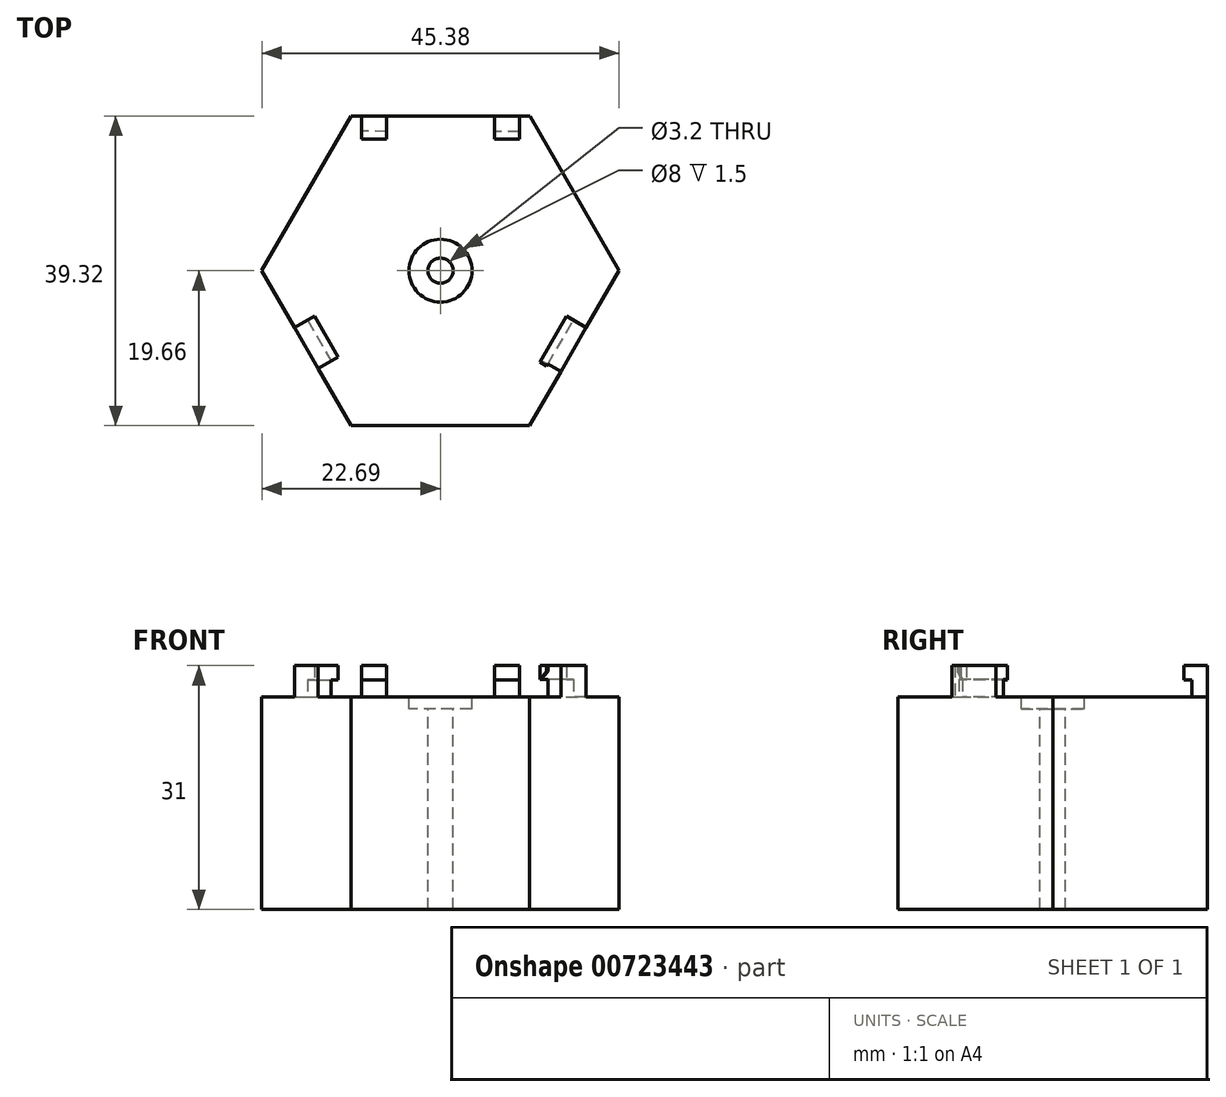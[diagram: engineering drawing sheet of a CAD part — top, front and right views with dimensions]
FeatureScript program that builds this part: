
annotation { "Feature Type Name" : "Feature", "Feature Type Description" : "" }
export const myFeature = defineFeature(function(context is Context, id is Id, definition is map)
    precondition{}
    {
        {
            var Q0;
            Q0=qCreatedBy(makeId("Top.planeOp"),FACE);
            var sketch = newSketch(context, id + "F0", { "sketchPlane" : qUnion([Q0])});
            skCircle(sketch, "E0.cCircle", {"center": v(0, 0) * mm, "radius": 17.65 * mm, "construction": true});
            skLineSegment(sketch, "E0.0", {"start": v(20.38, 0) * mm, "end": v(10.19, -17.66) * mm});
            skLineSegment(sketch, "E0.1", {"start": v(10.19, -17.66) * mm, "end": v(-10.2, -17.65) * mm});
            skLineSegment(sketch, "E0.2", {"start": v(-10.2, -17.65) * mm, "end": v(-20.38, 0) * mm});
            skLineSegment(sketch, "E0.3", {"start": v(-20.38, 0) * mm, "end": v(-10.19, 17.66) * mm});
            skLineSegment(sketch, "E0.4", {"start": v(-10.19, 17.66) * mm, "end": v(-6.75, 17.66) * mm});
            skLineSegment(sketch, "E0.5", {"start": v(10.2, 17.65) * mm, "end": v(20.39, 0) * mm});
            skPoint(sketch, "E0.0.midPoint", {"position": v(15.29, -8.83) * mm});
            skPoint(sketch, "E1", {"position": v(0, 17.65) * mm});
            skPoint(sketch, "E2", {"position": v(-10.19, 17.66) * mm});
            skPoint(sketch, "E3", {"position": v(10.2, 17.65) * mm});
            skLineSegment(sketch, "E4.top", {"start": v(6.75, 24.35) * mm, "end": v(-6.75, 24.35) * mm});
            skLineSegment(sketch, "E4.right", {"start": v(-6.75, 17.66) * mm, "end": v(-6.75, 24.35) * mm});
            skPoint(sketch, "E5.orphan", {"position": v(-6.75, 10.95) * mm});
            skLineSegment(sketch, "E6.trimOffspring", {"start": v(6.75, 17.65) * mm, "end": v(6.75, 24.35) * mm});
            skPoint(sketch, "E4.left.start.orphan", {"position": v(6.75, 10.95) * mm});
            skLineSegment(sketch, "E7.trimOffspring", {"start": v(6.75, 17.65) * mm, "end": v(10.2, 17.65) * mm});
            skLineSegment(sketch, "E8.trimOffspring", {"start": v(0, 17.65) * mm, "end": v(0, 17.65) * mm});
            skSolve(sketch);
        }
        {
            var Q0;
            Q0=qSketchRegion(id+"F0",true);
            extrude(context, id + "F1", {"entities" : qUnion([Q0]), "depth" : 1 * mm, "offsetDistance" : 25 * mm});
        }
        {
            var Q0;
            Q0=makeQuery(id+"F1.opExtrude","CAP_FACE",FACE,{"disambiguationData":[OSD([sQuery(id+"F0.wireOp",EDGE,"E0.0"),sQuery(id+"F0.wireOp",EDGE,"E0.1"),sQuery(id+"F0.wireOp",EDGE,"E0.2"),sQuery(id+"F0.wireOp",EDGE,"E0.3"),sQuery(id+"F0.wireOp",EDGE,"E0.4"),sQuery(id+"F0.wireOp",EDGE,"E0.5"),sQuery(id+"F0.wireOp",EDGE,"E4.top"),sQuery(id+"F0.wireOp",EDGE,"E4.right"),sQuery(id+"F0.wireOp",EDGE,"E6.trimOffspring"),sQuery(id+"F0.wireOp",EDGE,"E7.trimOffspring")])],"isStart":false});
            var sketch = newSketch(context, id + "F2", { "sketchPlane" : qUnion([Q0])});
            skPoint(sketch, "E9.0.midPoint", {"position": v(0, 13.44) * mm});
            skPoint(sketch, "E9.5.end.orphan", {"position": v(-7.76, 13.44) * mm});
            skPoint(sketch, "E10.orphan", {"position": v(-7.76, -13.44) * mm});
            skPoint(sketch, "E9.cCircle.center.orphan", {"position": v(0, 0) * mm});
            skPoint(sketch, "E9.0.end.orphan", {"position": v(7.76, 13.44) * mm});
            skLineSegment(sketch, "E11.0", {"start": v(18.94, 2.5) * mm, "end": v(16.44, 6.82) * mm});
            skLineSegment(sketch, "E11.3", {"start": v(-7.3, -17.65) * mm, "end": v(-2.3, -17.65) * mm});
            skLineSegment(sketch, "E11.5", {"start": v(-11.63, 15.16) * mm, "end": v(-14.13, 10.83) * mm});
            skLineSegment(sketch, "E12.0", {"start": v(14.61, 0) * mm, "end": v(12.11, 4.33) * mm});
            skLineSegment(sketch, "E12.3", {"start": v(-7.3, -12.65) * mm, "end": v(-2.3, -12.65) * mm});
            skLineSegment(sketch, "E12.5", {"start": v(-7.3, 12.66) * mm, "end": v(-9.8, 8.33) * mm});
            skLineSegment(sketch, "E13", {"start": v(-7.3, 12.66) * mm, "end": v(-11.63, 15.16) * mm});
            skLineSegment(sketch, "E14", {"start": v(-14.61, 0) * mm, "end": v(-18.94, 2.5) * mm});
            skLineSegment(sketch, "E15", {"start": v(7.3, 12.65) * mm, "end": v(11.64, 15.15) * mm});
            skLineSegment(sketch, "E16", {"start": v(14.61, 0) * mm, "end": v(18.94, 2.5) * mm});
            skLineSegment(sketch, "E17", {"start": v(-7.3, -12.65) * mm, "end": v(-7.3, -17.65) * mm});
            skLineSegment(sketch, "E18", {"start": v(7.3, -12.66) * mm, "end": v(7.3, -17.66) * mm});
            skLineSegment(sketch, "E19", {"start": v(7.3, -29.7) * mm, "end": v(6.52, -29.92) * mm});
            skLineSegment(sketch, "E20.right", {"start": v(-2.3, -12.65) * mm, "end": v(-2.3, -17.65) * mm});
            skLineSegment(sketch, "E21.bottom", {"start": v(7.3, -12.66) * mm, "end": v(2.3, -12.66) * mm});
            skLineSegment(sketch, "E21.top", {"start": v(7.3, -17.65) * mm, "end": v(2.3, -17.65) * mm});
            skLineSegment(sketch, "E21.left", {"start": v(7.3, -12.66) * mm, "end": v(7.3, -17.65) * mm});
            skLineSegment(sketch, "E21.right", {"start": v(2.3, -12.66) * mm, "end": v(2.3, -17.65) * mm});
            skPoint(sketch, "E22", {"position": v(12.11, 4.33) * mm});
            skPoint(sketch, "E23", {"position": v(9.8, 8.32) * mm});
            skPoint(sketch, "E24", {"position": v(-9.8, 8.33) * mm});
            skPoint(sketch, "E25", {"position": v(-12.11, 4.33) * mm});
            skLineSegment(sketch, "E26", {"start": v(-9.8, 8.33) * mm, "end": v(-14.13, 10.83) * mm});
            skLineSegment(sketch, "E27", {"start": v(-12.11, 4.33) * mm, "end": v(-16.44, 6.84) * mm});
            skLineSegment(sketch, "E28", {"start": v(9.8, 8.32) * mm, "end": v(14.14, 10.82) * mm});
            skLineSegment(sketch, "E29", {"start": v(12.11, 4.33) * mm, "end": v(20.39, 9.1) * mm});
            skLineSegment(sketch, "E30.trimOffspring", {"start": v(14.14, 10.82) * mm, "end": v(11.64, 15.15) * mm});
            skLineSegment(sketch, "E31.trimOffspring", {"start": v(9.8, 8.32) * mm, "end": v(7.3, 12.65) * mm});
            skLineSegment(sketch, "E32.trimOffspring", {"start": v(2.3, -17.65) * mm, "end": v(7.3, -17.66) * mm});
            skPoint(sketch, "E33.orphan", {"position": v(-7.3, -29.7) * mm});
            skLineSegment(sketch, "E34.trimOffspring", {"start": v(-12.11, 4.33) * mm, "end": v(-14.61, 0) * mm});
            skLineSegment(sketch, "E35.trimOffspring", {"start": v(-16.44, 6.84) * mm, "end": v(-18.94, 2.5) * mm});
            skSolve(sketch);
        }
        {
            var Q0;
            Q0=qSketchRegion(id+"F2",true);
            extrude(context, id + "F3", {"entities" : qUnion([Q0]), "operationType" : NewBodyOperationType.ADD, "depth" : 5 * mm, "offsetDistance" : 25 * mm});
        }
        {
            var Q0;
            Q0=qCreatedBy(makeId("Top.planeOp"),FACE);
            cPlane(context, id + "F4", {"entities" : qUnion([Q0]), "cplaneType" : CPlaneType.OFFSET, "offset" : .1 * mm, "oppositeDirection" : true, "width" : 150 * mm, "height" : 150 * mm});
        }
        {
            var Q0;
            Q0=qCreatedBy(id+"F4.planeOp",FACE);
            var sketch = newSketch(context, id + "F5", { "sketchPlane" : qUnion([Q0])});
            skLineSegment(sketch, "E36.2", {"start": v(8.75, 19.65) * mm, "end": v(11.35, 19.65) * mm});
            skLineSegment(sketch, "E36.4", {"start": v(-11.34, 19.66) * mm, "end": v(-8.75, 19.66) * mm});
            skLineSegment(sketch, "E36.5", {"start": v(-22.7, 0) * mm, "end": v(-11.34, 19.66) * mm});
            skLineSegment(sketch, "E36.6", {"start": v(11.35, 19.65) * mm, "end": v(22.7, 0) * mm});
            skLineSegment(sketch, "E36.7", {"start": v(22.7, 0) * mm, "end": v(11.34, -19.66) * mm});
            skLineSegment(sketch, "E36.8", {"start": v(11.34, -19.66) * mm, "end": v(-11.35, -19.65) * mm});
            skLineSegment(sketch, "E36.9", {"start": v(-11.35, -19.65) * mm, "end": v(-22.7, 0) * mm});
            skLineSegment(sketch, "E37", {"start": v(-8.75, 19.66) * mm, "end": v(8.75, 19.65) * mm});
            skSolve(sketch);
        }
        {
            var Q0;
            Q0=qSketchRegion(id+"F5",true);
            extrude(context, id + "F6", {"entities" : qUnion([Q0]), "operationType" : NewBodyOperationType.ADD, "oppositeDirection" : true, "depth" : 2 * mm, "offsetDistance" : 25 * mm});
        }
        {
            var Q0;
            Q0=makeQuery(id+"F6.opExtrude","CAP_FACE",FACE,{"disambiguationData":[OSD([sQuery(id+"F5.wireOp",EDGE,"E36.2"),sQuery(id+"F5.wireOp",EDGE,"E36.4"),sQuery(id+"F5.wireOp",EDGE,"E36.5"),sQuery(id+"F5.wireOp",EDGE,"E36.6"),sQuery(id+"F5.wireOp",EDGE,"E36.7"),sQuery(id+"F5.wireOp",EDGE,"E36.8"),sQuery(id+"F5.wireOp",EDGE,"E36.9"),sQuery(id+"F5.wireOp",EDGE,"E37")])],"isStart":true});
            var sketch = newSketch(context, id + "F7", { "sketchPlane" : qUnion([Q0])});
            skLineSegment(sketch, "E38.0", {"start": v(17.12, -5.26) * mm, "end": v(15.12, -8.73) * mm});
            skLineSegment(sketch, "E39.0", {"start": v(-13.12, -12.19) * mm, "end": v(-17.12, -5.26) * mm});
            skLineSegment(sketch, "E40.0", {"start": v(-10.14, 17.46) * mm, "end": v(-7.14, 17.46) * mm});
            skLineSegment(sketch, "E41", {"start": v(-7.14, 17.46) * mm, "end": v(-7.14, 19.66) * mm});
            skLineSegment(sketch, "E42", {"start": v(-10.14, 17.46) * mm, "end": v(-10.14, 19.66) * mm});
            skPoint(sketch, "E43.end.orphan", {"position": v(7.22, 19.66) * mm});
            skPoint(sketch, "E44.end.orphan", {"position": v(10.18, 19.66) * mm});
            skLineSegment(sketch, "E45.MirrorCS", {"start": v(10.14, 17.46) * mm, "end": v(10.14, 19.66) * mm});
            skLineSegment(sketch, "E46.MirrorCS", {"start": v(7.14, 17.46) * mm, "end": v(7.14, 19.66) * mm});
            skLineSegment(sketch, "E47.MirrorCS", {"start": v(10.14, 17.46) * mm, "end": v(7.14, 17.46) * mm});
            skLineSegment(sketch, "E48", {"start": v(-10.14, 19.66) * mm, "end": v(-7.14, 19.66) * mm});
            skLineSegment(sketch, "E49", {"start": v(7.14, 19.66) * mm, "end": v(10.14, 19.66) * mm});
            skLineSegment(sketch, "E50", {"start": v(-19.02, -6.36) * mm, "end": v(-17.12, -5.26) * mm});
            skLineSegment(sketch, "E51", {"start": v(-15.03, -13.29) * mm, "end": v(-13.12, -12.19) * mm});
            skPoint(sketch, "E52.orphan", {"position": v(-17.02, -9.82) * mm});
            skLineSegment(sketch, "E53", {"start": v(-15.03, -13.29) * mm, "end": v(-19.02, -6.36) * mm});
            skLineSegment(sketch, "E54.MirrorCS", {"start": v(15.03, -13.29) * mm, "end": v(19.02, -6.36) * mm});
            skLineSegment(sketch, "E55.MirrorCS", {"start": v(19.02, -6.36) * mm, "end": v(17.12, -5.26) * mm});
            skLineSegment(sketch, "E56.MirrorCS", {"start": v(15.03, -13.29) * mm, "end": v(13.12, -12.19) * mm});
            skLineSegment(sketch, "E57.MirrorCS", {"start": v(13.12, -12.19) * mm, "end": v(17.12, -5.26) * mm});
            skPoint(sketch, "E58.MirrorP", {"position": v(17.02, -9.82) * mm});
            skSolve(sketch);
        }
        {
            var Q0;
            Q0=qSketchRegion(id+"F7",true);
            extrude(context, id + "F8", {"entities" : qUnion([Q0]), "depth" : 4 * mm, "offsetDistance" : 25 * mm});
        }
        {
            var Q0;
            Q0=makeQuery(id+"F8.opExtrude","CAP_EDGE",EDGE,{"disambiguationData":[OSD([sQuery(id+"F7.wireOp",EDGE,"E39.0")])],"isStart":true});
            var Q1;
            Q1=makeQuery(id+"F8.opExtrude","CAP_EDGE",EDGE,{"disambiguationData":[OSD([sQuery(id+"F7.wireOp",EDGE,"E47.MirrorCS")])],"isStart":true});
            var Q2;
            Q2=makeQuery(id+"F8.opExtrude","CAP_EDGE",EDGE,{"disambiguationData":[OSD([sQuery(id+"F7.wireOp",EDGE,"E40.0")])],"isStart":true});
            var Q3;
            Q3=makeQuery(id+"F8.opExtrude","CAP_EDGE",EDGE,{"disambiguationData":[OSD([sQuery(id+"F7.wireOp",EDGE,"E57.MirrorCS")])],"isStart":true});
            chamfer(context, id + "F9", {"entities" : qUnion([Q0, Q1, Q2, Q3]), "chamferType" : ChamferType.TWO_OFFSETS, "width1" : 4 * mm, "oppositeDirection" : false, "width2" : .4 * mm, "tangentPropagation" : true});
        }
        {
            var Q0;
            Q0=makeQuery(id+"F8.opExtrude","SWEPT_BODY",BODY,{"disambiguationData":[OSD([sQuery(id+"F7.wireOp",EDGE,"E54.MirrorCS"),sQuery(id+"F7.wireOp",EDGE,"E55.MirrorCS"),sQuery(id+"F7.wireOp",EDGE,"E56.MirrorCS"),sQuery(id+"F7.wireOp",EDGE,"E57.MirrorCS")])]});
            var Q1;
            Q1=makeQuery(id+"F8.opExtrude","SWEPT_BODY",BODY,{"disambiguationData":[OSD([sQuery(id+"F7.wireOp",EDGE,"E45.MirrorCS"),sQuery(id+"F7.wireOp",EDGE,"E46.MirrorCS"),sQuery(id+"F7.wireOp",EDGE,"E47.MirrorCS"),sQuery(id+"F7.wireOp",EDGE,"E49")])]});
            var Q2;
            Q2=makeQuery(id+"F8.opExtrude","SWEPT_BODY",BODY,{"disambiguationData":[OSD([sQuery(id+"F7.wireOp",EDGE,"E40.0"),sQuery(id+"F7.wireOp",EDGE,"E41"),sQuery(id+"F7.wireOp",EDGE,"E42"),sQuery(id+"F7.wireOp",EDGE,"E48")])]});
            var Q3;
            Q3=makeQuery(id+"F8.opExtrude","SWEPT_BODY",BODY,{"disambiguationData":[OSD([sQuery(id+"F7.wireOp",EDGE,"E39.0"),sQuery(id+"F7.wireOp",EDGE,"E50"),sQuery(id+"F7.wireOp",EDGE,"E51"),sQuery(id+"F7.wireOp",EDGE,"E53")])]});
            deleteBodies(context, id + "F10", {"entities" : qUnion([Q0, Q1, Q2, Q3])});
        }
        {
            var Q0;
            Q0=makeQuery(id+"F6.opExtrude","CAP_FACE",FACE,{"disambiguationData":[OSD([sQuery(id+"F5.wireOp",EDGE,"E36.2"),sQuery(id+"F5.wireOp",EDGE,"E36.4"),sQuery(id+"F5.wireOp",EDGE,"E36.5"),sQuery(id+"F5.wireOp",EDGE,"E36.6"),sQuery(id+"F5.wireOp",EDGE,"E36.7"),sQuery(id+"F5.wireOp",EDGE,"E36.8"),sQuery(id+"F5.wireOp",EDGE,"E36.9"),sQuery(id+"F5.wireOp",EDGE,"E37")])],"isStart":true});
            var sketch = newSketch(context, id + "F11", { "sketchPlane" : qUnion([Q0])});
            skLineSegment(sketch, "E59.0", {"start": v(10.05, 17.7) * mm, "end": v(6.85, 17.7) * mm});
            skLineSegment(sketch, "E59.1", {"start": v(-16.88, -6.27) * mm, "end": v(-13.88, -11.47) * mm});
            skLineSegment(sketch, "E59.4", {"start": v(13.64, -11.88) * mm, "end": v(16.87, -6.28) * mm});
            skLineSegment(sketch, "E60", {"start": v(-10.04, 17.7) * mm, "end": v(-10.04, 19.66) * mm});
            skLineSegment(sketch, "E61", {"start": v(10.05, 17.7) * mm, "end": v(10.05, 19.65) * mm});
            skLineSegment(sketch, "E62", {"start": v(-6.84, 17.7) * mm, "end": v(-6.84, 19.66) * mm});
            skLineSegment(sketch, "E63", {"start": v(6.85, 17.7) * mm, "end": v(6.85, 19.66) * mm});
            skLineSegment(sketch, "E64", {"start": v(-15.52, -12.42) * mm, "end": v(-13.88, -11.47) * mm});
            skLineSegment(sketch, "E65", {"start": v(-18.52, -7.22) * mm, "end": v(-16.88, -6.27) * mm});
            skLineSegment(sketch, "E66", {"start": v(18.52, -7.23) * mm, "end": v(16.87, -6.28) * mm});
            skLineSegment(sketch, "E67", {"start": v(15.28, -12.83) * mm, "end": v(13.64, -11.88) * mm});
            skPoint(sketch, "E68.orphan", {"position": v(-14.94, -5.16) * mm});
            skPoint(sketch, "E69.orphan", {"position": v(-11.35, -10.01) * mm});
            skPoint(sketch, "E70.orphan", {"position": v(14.92, -5.16) * mm});
            skPoint(sketch, "E71.start.orphan", {"position": v(17.02, -9.83) * mm});
            skLineSegment(sketch, "E72.trimOffspring", {"start": v(-6.84, 17.7) * mm, "end": v(-10.04, 17.7) * mm});
            skPoint(sketch, "E73.start.orphan", {"position": v(-17.02, -9.82) * mm});
            skLineSegment(sketch, "E74", {"start": v(-15.52, -12.42) * mm, "end": v(-18.52, -7.22) * mm});
            skLineSegment(sketch, "E75", {"start": v(15.28, -12.83) * mm, "end": v(18.52, -7.23) * mm});
            skLineSegment(sketch, "E76", {"start": v(10.05, 19.65) * mm, "end": v(6.85, 19.66) * mm});
            skLineSegment(sketch, "E77", {"start": v(-6.84, 19.66) * mm, "end": v(-10.04, 19.66) * mm});
            skSolve(sketch);
        }
        {
            var Q0;
            Q0=qSketchRegion(id+"F11",true);
            extrude(context, id + "F12", {"entities" : qUnion([Q0]), "operationType" : NewBodyOperationType.ADD, "depth" : 4 * mm, "offsetDistance" : 25 * mm});
        }
        {
            var Q0;
            Q0=makeQuery(id+"F12.opExtrude","SWEPT_FACE",FACE,{"disambiguationData":[OSD([sQuery(id+"F11.wireOp",EDGE,"E72.trimOffspring")])]});
            var sketch = newSketch(context, id + "F13", { "sketchPlane" : qUnion([Q0])});
            skLineSegment(sketch, "E78.bottom", {"start": v(-10.05, 3.9) * mm, "end": v(-6.85, 3.9) * mm});
            skLineSegment(sketch, "E78.top", {"start": v(-10.05, 2.05) * mm, "end": v(-6.85, 2.05) * mm});
            skLineSegment(sketch, "E78.left", {"start": v(-10.05, 3.9) * mm, "end": v(-10.05, 2.05) * mm});
            skLineSegment(sketch, "E78.right", {"start": v(-6.85, 3.9) * mm, "end": v(-6.85, 2.05) * mm});
            skSolve(sketch);
        }
        {
            var Q0;
            Q0=qSketchRegion(id+"F13",true);
            extrude(context, id + "F14", {"entities" : qUnion([Q0]), "operationType" : NewBodyOperationType.ADD, "depth" : 1 * mm, "offsetDistance" : 25 * mm});
        }
        {
            var Q0;
            Q0=makeQuery(id+"F12.opExtrude","SWEPT_FACE",FACE,{"disambiguationData":[OSD([sQuery(id+"F11.wireOp",EDGE,"E59.0")])]});
            var sketch = newSketch(context, id + "F15", { "sketchPlane" : qUnion([Q0])});
            skLineSegment(sketch, "E79.bottom", {"start": v(6.84, 3.9) * mm, "end": v(10.05, 3.9) * mm});
            skLineSegment(sketch, "E79.top", {"start": v(6.84, 2.07) * mm, "end": v(10.05, 2.07) * mm});
            skLineSegment(sketch, "E79.left", {"start": v(6.84, 3.9) * mm, "end": v(6.84, 2.07) * mm});
            skLineSegment(sketch, "E79.right", {"start": v(10.05, 3.9) * mm, "end": v(10.05, 2.07) * mm});
            skSolve(sketch);
        }
        {
            var Q0;
            Q0=qSketchRegion(id+"F15",true);
            extrude(context, id + "F16", {"entities" : qUnion([Q0]), "operationType" : NewBodyOperationType.ADD, "depth" : 1 * mm, "offsetDistance" : 25 * mm});
        }
        {
            var Q0;
            Q0=makeQuery(id+"F12.opExtrude","SWEPT_FACE",FACE,{"disambiguationData":[OSD([sQuery(id+"F11.wireOp",EDGE,"E59.4")])]});
            var sketch = newSketch(context, id + "F17", { "sketchPlane" : qUnion([Q0])});
            skLineSegment(sketch, "E80.bottom", {"start": v(-3, 3.9) * mm, "end": v(3.75, 3.9) * mm});
            skLineSegment(sketch, "E80.top", {"start": v(-3, 2.13) * mm, "end": v(3.75, 2.13) * mm});
            skLineSegment(sketch, "E80.left", {"start": v(-3, 3.9) * mm, "end": v(-3, 2.13) * mm});
            skLineSegment(sketch, "E80.right", {"start": v(3.75, 3.9) * mm, "end": v(3.75, 2.13) * mm});
            skSolve(sketch);
        }
        {
            var Q0;
            Q0=qSketchRegion(id+"F17",true);
            extrude(context, id + "F18", {"entities" : qUnion([Q0]), "operationType" : NewBodyOperationType.ADD, "depth" : 1 * mm, "offsetDistance" : 25 * mm});
        }
        {
            var Q0;
            Q0=makeQuery(id+"F12.opExtrude","SWEPT_FACE",FACE,{"disambiguationData":[OSD([sQuery(id+"F11.wireOp",EDGE,"E59.1")])]});
            var sketch = newSketch(context, id + "F19", { "sketchPlane" : qUnion([Q0])});
            skLineSegment(sketch, "E81.bottom", {"start": v(3, 3.9) * mm, "end": v(-3, 3.9) * mm});
            skLineSegment(sketch, "E81.top", {"start": v(3, 2.1) * mm, "end": v(-3, 2.1) * mm});
            skLineSegment(sketch, "E81.left", {"start": v(3, 3.9) * mm, "end": v(3, 2.1) * mm});
            skLineSegment(sketch, "E81.right", {"start": v(-3, 3.9) * mm, "end": v(-3, 2.1) * mm});
            skSolve(sketch);
        }
        {
            var Q0;
            Q0=qSketchRegion(id+"F19",true);
            extrude(context, id + "F20", {"entities" : qUnion([Q0]), "operationType" : NewBodyOperationType.ADD, "depth" : 1 * mm, "offsetDistance" : 25 * mm});
        }
        {
            var Q0;
            Q0=makeQuery(id+"F16.opExtrude","CAP_EDGE",EDGE,{"disambiguationData":[OSD([sQuery(id+"F15.wireOp",EDGE,"E79.top")])],"isStart":true});
            var Q1;
            {var subQ0=sQuery(id+"F17.wireOp",EDGE,"E80.top");Q1=makeQuery(id+"F18.boolean.opBoolean","SPLIT",EDGE,{"disambiguationData":[topologyDisambiguationEdgeConnected([makeQuery(id+"F12.opExtrude","SWEPT_FACE",FACE,{"disambiguationData":[OSD([sQuery(id+"F11.wireOp",EDGE,"E59.4")])]})])],"derivedFrom":makeQuery(id+"F18.opExtrude","CAP_EDGE",EDGE,{"disambiguationData":[OSD([subQ0])],"isStart":true})});}
            var Q2;
            Q2=makeQuery(id+"F14.opExtrude","CAP_EDGE",EDGE,{"disambiguationData":[OSD([sQuery(id+"F13.wireOp",EDGE,"E78.top")])],"isStart":true});
            var Q3;
            Q3=makeQuery(id+"F20.opExtrude","CAP_EDGE",EDGE,{"disambiguationData":[OSD([sQuery(id+"F19.wireOp",EDGE,"E81.top")])],"isStart":true});
            chamfer(context, id + "F21", {"entities" : qUnion([Q0, Q1, Q2, Q3]), "width" : 1 * mm, "tangentPropagation" : true});
        }
        {
            var Q0;
            Q0=makeQuery(id+"F1.opExtrude","SWEPT_BODY",BODY,{"disambiguationData":[OSD([sQuery(id+"F0.wireOp",EDGE,"E0.0"),sQuery(id+"F0.wireOp",EDGE,"E0.1"),sQuery(id+"F0.wireOp",EDGE,"E0.2"),sQuery(id+"F0.wireOp",EDGE,"E0.3"),sQuery(id+"F0.wireOp",EDGE,"E0.4"),sQuery(id+"F0.wireOp",EDGE,"E0.5"),sQuery(id+"F0.wireOp",EDGE,"E4.top"),sQuery(id+"F0.wireOp",EDGE,"E4.right"),sQuery(id+"F0.wireOp",EDGE,"E6.trimOffspring"),sQuery(id+"F0.wireOp",EDGE,"E7.trimOffspring")])]});
            deleteBodies(context, id + "F22", {"entities" : qUnion([Q0])});
        }
        {
            var Q0;
            Q0=makeQuery(id+"F6.opExtrude","CAP_FACE",FACE,{"disambiguationData":[OSD([sQuery(id+"F5.wireOp",EDGE,"E36.2"),sQuery(id+"F5.wireOp",EDGE,"E36.4"),sQuery(id+"F5.wireOp",EDGE,"E36.5"),sQuery(id+"F5.wireOp",EDGE,"E36.6"),sQuery(id+"F5.wireOp",EDGE,"E36.7"),sQuery(id+"F5.wireOp",EDGE,"E36.8"),sQuery(id+"F5.wireOp",EDGE,"E36.9"),sQuery(id+"F5.wireOp",EDGE,"E37")])],"isStart":true});
            var sketch = newSketch(context, id + "F23", { "sketchPlane" : qUnion([Q0])});
            skCircle(sketch, "E82", {"center": v(0, 0) * mm, "radius": 1.6 * mm});
            skSolve(sketch);
        }
        {
            var Q0;
            Q0=qSketchRegion(id+"F23",true);
            extrude(context, id + "F24", {"entities" : qUnion([Q0]), "operationType" : NewBodyOperationType.REMOVE, "endBound" : BoundingType.THROUGH_ALL, "oppositeDirection" : true, "depth" : 25 * mm, "offsetDistance" : 25 * mm});
        }
        {
            var Q0;
            Q0=makeQuery(id+"F6.opExtrude","CAP_FACE",FACE,{"disambiguationData":[OSD([sQuery(id+"F5.wireOp",EDGE,"E36.2"),sQuery(id+"F5.wireOp",EDGE,"E36.4"),sQuery(id+"F5.wireOp",EDGE,"E36.5"),sQuery(id+"F5.wireOp",EDGE,"E36.6"),sQuery(id+"F5.wireOp",EDGE,"E36.7"),sQuery(id+"F5.wireOp",EDGE,"E36.8"),sQuery(id+"F5.wireOp",EDGE,"E36.9"),sQuery(id+"F5.wireOp",EDGE,"E37")])],"isStart":true});
            var sketch = newSketch(context, id + "F25", { "sketchPlane" : qUnion([Q0])});
            skCircle(sketch, "E83", {"center": v(0, 0) * mm, "radius": 4 * mm});
            skSolve(sketch);
        }
        {
            var Q0;
            Q0=qSketchRegion(id+"F25",true);
            extrude(context, id + "F26", {"entities" : qUnion([Q0]), "operationType" : NewBodyOperationType.REMOVE, "oppositeDirection" : true, "depth" : 1.5 * mm, "offsetDistance" : 25 * mm});
        }
        {
            var Q0;
            Q0=makeQuery(id+"F6.opExtrude","CAP_FACE",FACE,{"disambiguationData":[OSD([sQuery(id+"F5.wireOp",EDGE,"E36.2"),sQuery(id+"F5.wireOp",EDGE,"E36.4"),sQuery(id+"F5.wireOp",EDGE,"E36.5"),sQuery(id+"F5.wireOp",EDGE,"E36.6"),sQuery(id+"F5.wireOp",EDGE,"E36.7"),sQuery(id+"F5.wireOp",EDGE,"E36.8"),sQuery(id+"F5.wireOp",EDGE,"E36.9"),sQuery(id+"F5.wireOp",EDGE,"E37")])],"isStart":false});
            extrude(context, id + "F27", {"entities" : qUnion([Q0]), "operationType" : NewBodyOperationType.ADD, "depth" : 25 * mm, "offsetDistance" : 25 * mm});
        }
    });
